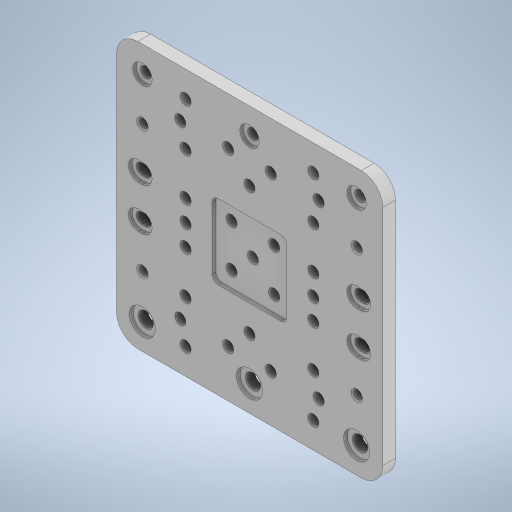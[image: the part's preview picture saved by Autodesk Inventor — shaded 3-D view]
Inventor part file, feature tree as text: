
AUTODESK INVENTOR PART (.ipt)
format: ipt  version: 2023.2 (Build 272271000, 271)  size: 371,712 bytes
history: native  units: mm
features: other x1, chamfer x1
ambient origin geometry x8: Origin, YZ Plane, XZ Plane, XY Plane, X Axis, Y Axis, Z Axis, Center Point
bodies: Solid1 (feature_tree)
feature tree (2):
  other  "C-Beam Gantry Plate XLarge.STEP"
  chamfer  "Chamfer1"  [1 undecoded]
note: 1 required parameter value undecoded (feature->parameter linkage not recoverable at this tier; creation-order binding heuristic only, values carry confidence <= 0.55)
